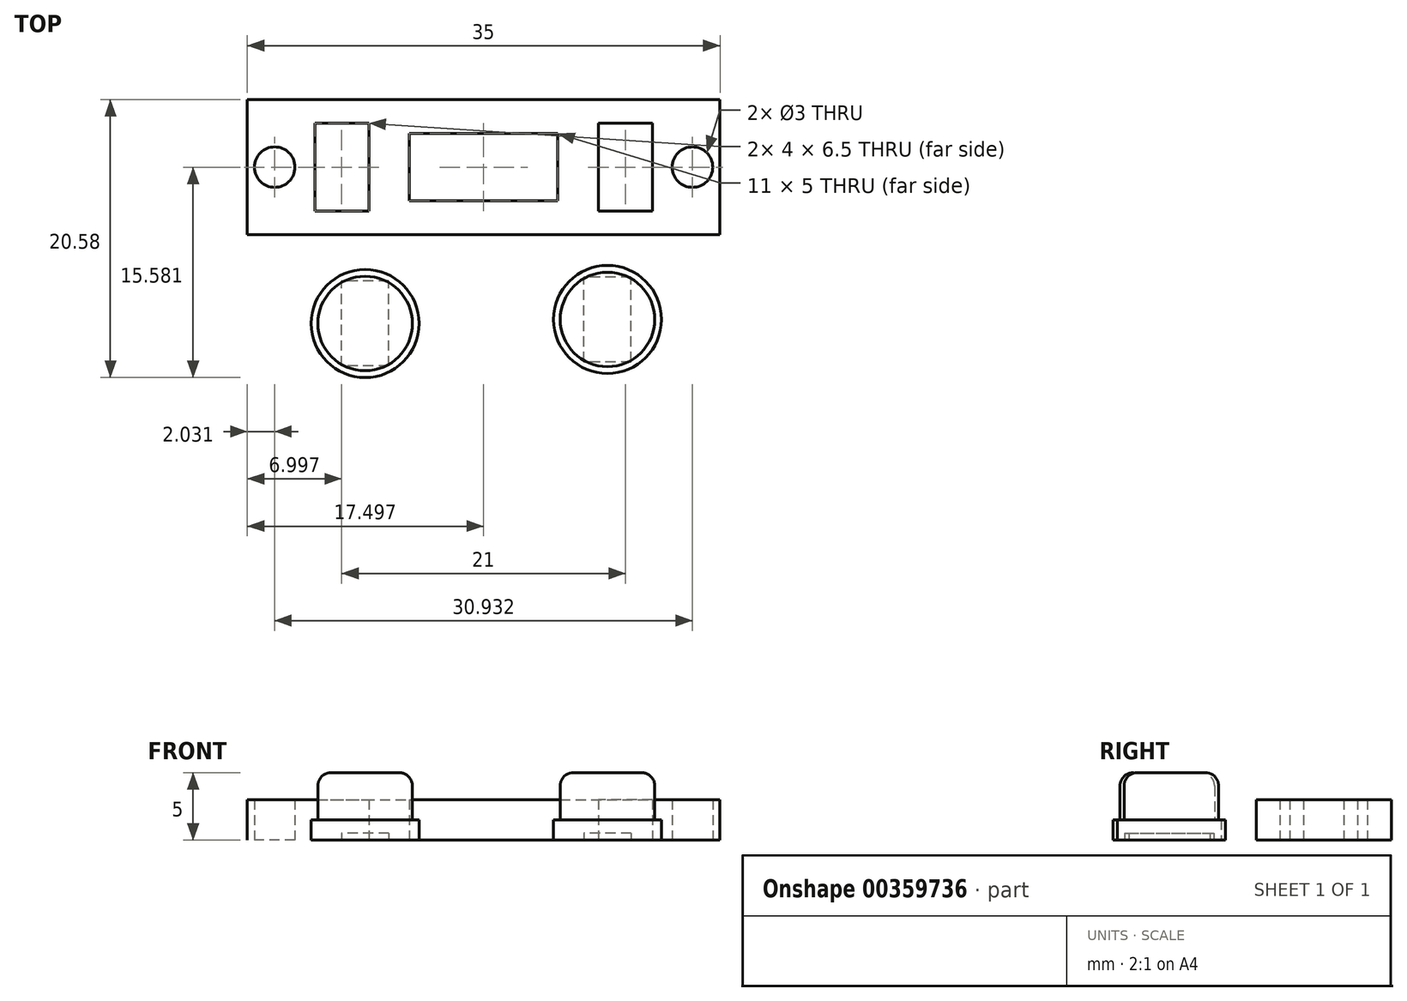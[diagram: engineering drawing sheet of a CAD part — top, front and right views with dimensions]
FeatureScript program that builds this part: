
annotation { "Feature Type Name" : "Feature", "Feature Type Description" : "" }
export const myFeature = defineFeature(function(context is Context, id is Id, definition is map)
    precondition{}
    {
        {
            var Q0;
            Q0=qCreatedBy(makeId("Top.planeOp"),FACE);
            var sketch = newSketch(context, id + "F0", { "sketchPlane" : qUnion([Q0])});
            skLineSegment(sketch, "E0.bottom", {"start": v(-28.5, 10.33) * mm, "end": v(6.5, 10.33) * mm});
            skLineSegment(sketch, "E0.top", {"start": v(-28.5, 0.33) * mm, "end": v(6.5, 0.33) * mm});
            skLineSegment(sketch, "E0.left", {"start": v(-28.5, 10.33) * mm, "end": v(-28.5, 0.33) * mm});
            skLineSegment(sketch, "E0.right", {"start": v(6.5, 10.33) * mm, "end": v(6.5, 0.33) * mm});
            skPoint(sketch, "E1", {"position": v(-11, 10.33) * mm});
            skPoint(sketch, "E2", {"position": v(-28.5, 5.33) * mm});
            skLineSegment(sketch, "E3", {"start": v(-43.94, 5.33) * mm, "end": v(29.9, 5.33) * mm, "construction": true});
            skLineSegment(sketch, "E4", {"start": v(-11, 23.92) * mm, "end": v(-11, -17.76) * mm, "construction": true});
            skLineSegment(sketch, "E5.bottom", {"start": v(-23.5, 2.08) * mm, "end": v(1.5, 2.08) * mm, "construction": true});
            skLineSegment(sketch, "E5.top", {"start": v(-23.5, 8.58) * mm, "end": v(1.5, 8.58) * mm, "construction": true});
            skLineSegment(sketch, "E5.left", {"start": v(-23.5, 2.08) * mm, "end": v(-23.5, 8.58) * mm, "construction": true});
            skLineSegment(sketch, "E5.right", {"start": v(1.5, 2.08) * mm, "end": v(1.5, 8.58) * mm, "construction": true});
            skPoint(sketch, "E6", {"position": v(-11, 8.58) * mm});
            skPoint(sketch, "E7", {"position": v(-23.5, 5.33) * mm});
            skLineSegment(sketch, "E8.bottom", {"start": v(-23.5, 8.58) * mm, "end": v(-19.5, 8.58) * mm});
            skLineSegment(sketch, "E8.top", {"start": v(-23.5, 2.08) * mm, "end": v(-19.5, 2.08) * mm});
            skLineSegment(sketch, "E8.left", {"start": v(-23.5, 8.58) * mm, "end": v(-23.5, 2.08) * mm});
            skLineSegment(sketch, "E8.right", {"start": v(-19.5, 8.58) * mm, "end": v(-19.5, 2.08) * mm});
            skLineSegment(sketch, "E9.bottom", {"start": v(1.5, 8.58) * mm, "end": v(-2.5, 8.58) * mm});
            skLineSegment(sketch, "E9.top", {"start": v(1.5, 2.08) * mm, "end": v(-2.5, 2.08) * mm});
            skLineSegment(sketch, "E9.left", {"start": v(1.5, 8.58) * mm, "end": v(1.5, 2.08) * mm});
            skLineSegment(sketch, "E9.right", {"start": v(-2.5, 8.58) * mm, "end": v(-2.5, 2.08) * mm});
            skCircle(sketch, "E10", {"center": v(-26.46, 5.33) * mm, "radius": 1.5 * mm});
            skCircle(sketch, "E11.MirrorC", {"center": v(4.47, 5.33) * mm, "radius": 1.5 * mm});
            skLineSegment(sketch, "E12.bottom", {"start": v(-16.5, 7.83) * mm, "end": v(-5.5, 7.83) * mm});
            skLineSegment(sketch, "E12.top", {"start": v(-16.5, 2.83) * mm, "end": v(-5.5, 2.83) * mm});
            skLineSegment(sketch, "E12.left", {"start": v(-16.5, 7.83) * mm, "end": v(-16.5, 2.83) * mm});
            skLineSegment(sketch, "E12.right", {"start": v(-5.5, 7.83) * mm, "end": v(-5.5, 2.83) * mm});
            skPoint(sketch, "E13", {"position": v(-11, 2.83) * mm});
            skPoint(sketch, "E14", {"position": v(-16.5, 5.33) * mm});
            skSolve(sketch);
        }
        {
            var Q0;
            Q0 = qSketchRegion(id + "F0", true);
            extrude(context, id + "F1", {"entities" : qUnion([Q0]), "depth" : 3 * mm, "offsetDistance" : 25 * mm});
        }
        {
            var Q0;
            Q0=qCreatedBy(makeId("Top.planeOp"),FACE);
            var sketch = newSketch(context, id + "F2", { "sketchPlane" : qUnion([Q0])});
            skCircle(sketch, "E15", {"center": v(-11.56, -8.85) * mm, "radius": 3.5 * mm});
            skSolve(sketch);
        }
        {
            var Q0;
            Q0=makeQuery(id+"F2.imprint","IMPRINT",FACE,{"disambiguationData":[TD([[makeQuery(id+"F2.imprint","IMPRINT",EDGE,{"derivedFrom":sQuery(id+"F2.wireOp",EDGE,"E15")}),1.0]])]});
            extrude(context, id + "F3", {"entities" : qUnion([Q0]), "depth" : 5 * mm, "offsetDistance" : 25 * mm});
        }
        {
            var Q0;
            Q0=makeQuery(id+"F3.opExtrude","CAP_EDGE",EDGE,{"disambiguationData":[OSD([sQuery(id+"F2.wireOp",EDGE,"E15")])],"isStart":false});
            fillet(context, id + "F4", {"entities" : qUnion([Q0]), "radius" : 1 * mm, "tangentPropagation" : true, "allowEdgeOverflow" : false});
        }
        {
            var Q0;
            Q0=makeQuery(id+"F3.opExtrude","CAP_FACE",FACE,{"disambiguationData":[OSD([sQuery(id+"F2.wireOp",EDGE,"E15")])],"isStart":true});
            var sketch = newSketch(context, id + "F5", { "sketchPlane" : qUnion([Q0])});
            skCircle(sketch, "E16", {"center": v(-11.56, 8.85) * mm, "radius": 4 * mm});
            skSolve(sketch);
        }
        {
            var Q0;
            Q0 = qSketchRegion(id + "F5", true);
            extrude(context, id + "F6", {"entities" : qUnion([Q0]), "operationType" : NewBodyOperationType.ADD, "oppositeDirection" : true, "depth" : 1.5 * mm, "offsetDistance" : 25 * mm});
        }
        {
            var Q0;
            Q0=makeQuery(id+"F6.boolean.opBoolean","MERGE",FACE,{"derivedFrom":[makeQuery(id+"F3.opExtrude","CAP_FACE",FACE,{"disambiguationData":[OSD([sQuery(id+"F2.wireOp",EDGE,"E15")])],"isStart":true}),makeQuery(id+"F6.opExtrude","CAP_FACE",FACE,{"disambiguationData":[OSD([sQuery(id+"F5.wireOp",EDGE,"E16")])],"isStart":true})]});
            var sketch = newSketch(context, id + "F7", { "sketchPlane" : qUnion([Q0])});
            skCircle(sketch, "E17.0", {"center": v(-11.56, 8.85) * mm, "radius": 4 * mm});
            skLineSegment(sketch, "E18.bottom", {"start": v(-9.81, 12) * mm, "end": v(-13.31, 12) * mm});
            skLineSegment(sketch, "E18.top", {"start": v(-9.81, 5.7) * mm, "end": v(-13.31, 5.7) * mm});
            skLineSegment(sketch, "E18.left", {"start": v(-9.81, 12) * mm, "end": v(-9.81, 5.7) * mm});
            skLineSegment(sketch, "E18.right", {"start": v(-13.31, 12) * mm, "end": v(-13.31, 5.7) * mm});
            skSolve(sketch);
        }
        {
            var Q0;
            Q0=makeQuery(id+"F7.imprint","IMPRINT",FACE,{"disambiguationData":[TD([[makeQuery(id+"F7.imprint","IMPRINT",EDGE,{"derivedFrom":sQuery(id+"F7.wireOp",EDGE,"E18.bottom")}),1.0]])]});
            extrude(context, id + "F8", {"entities" : qUnion([Q0]), "operationType" : NewBodyOperationType.REMOVE, "oppositeDirection" : true, "depth" : .5 * mm, "offsetDistance" : 25 * mm});
        }
        {
            var Q0;
            Q0=makeQuery(id+"F3.opExtrude","SWEPT_BODY",BODY,{"disambiguationData":[OSD([sQuery(id+"F2.wireOp",EDGE,"E15")])]});
            transform(context, id + "F9", {"entities" : qUnion([Q0]), "transformType" : TransformType.TRANSLATION_3D, "dx" : 9.74 * mm, "dy" : 2.9 * mm, "dz" : 0 * mm, "makeCopy" : true});
        }
        {
            var Q0;
            Q0=makeQuery(id+"F3.opExtrude","SWEPT_BODY",BODY,{"disambiguationData":[OSD([sQuery(id+"F2.wireOp",EDGE,"E15")])]});
            transform(context, id + "F10", {"entities" : qUnion([Q0]), "transformType" : TransformType.TRANSLATION_3D, "dx" : -8.2 * mm, "dy" : 2.6 * mm, "dz" : 0 * mm, "makeCopy" : false});
        }
    });
